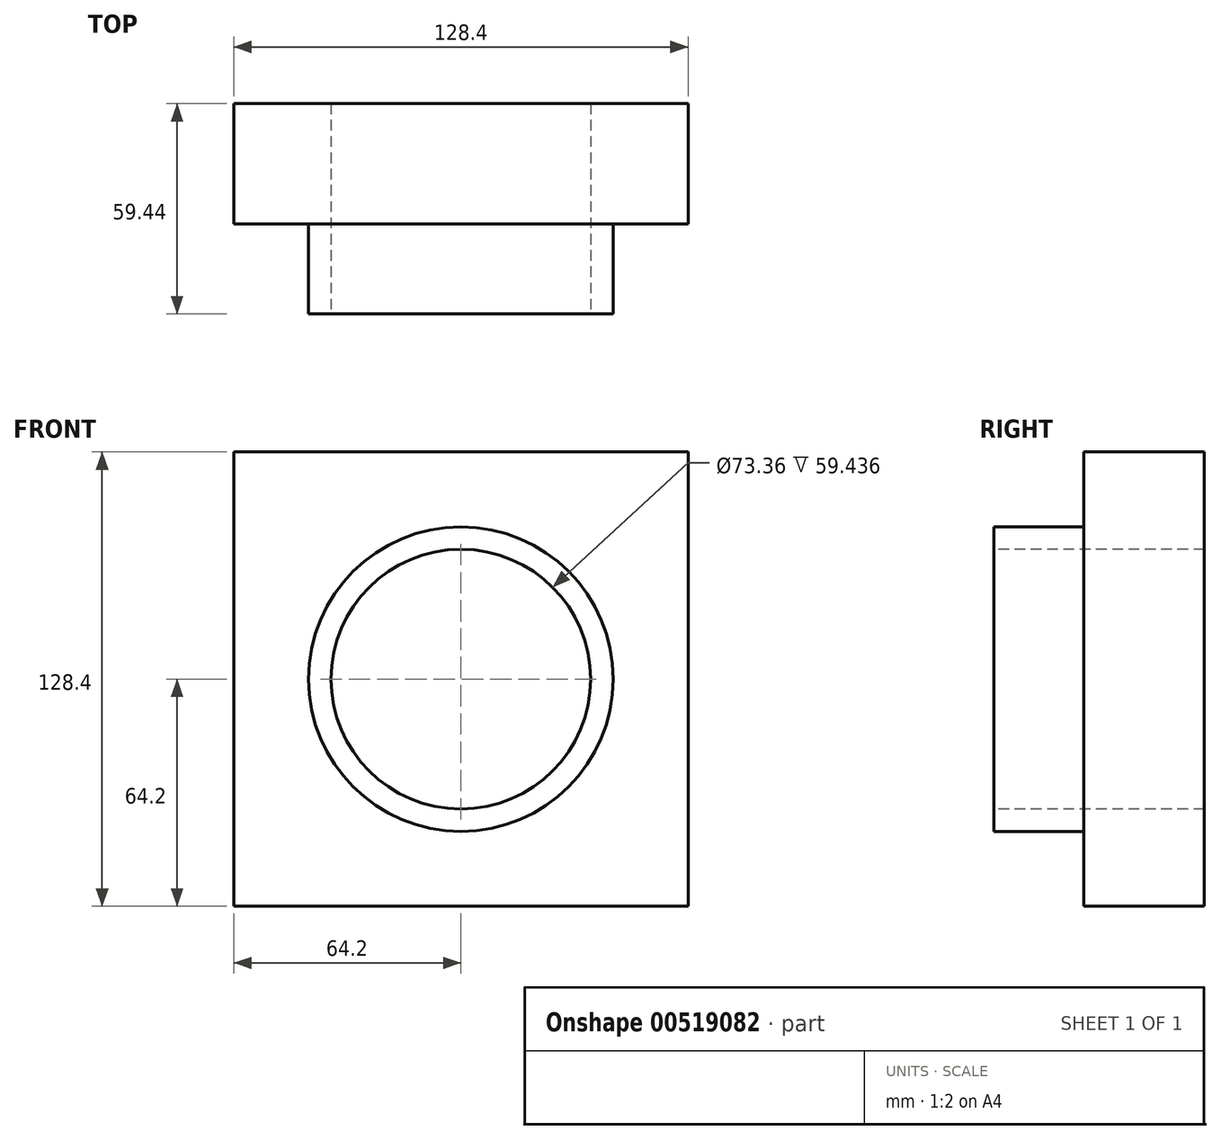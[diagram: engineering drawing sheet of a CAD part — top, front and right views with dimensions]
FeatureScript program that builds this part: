
annotation { "Feature Type Name" : "Feature", "Feature Type Description" : "" }
export const myFeature = defineFeature(function(context is Context, id is Id, definition is map)
    precondition{}
    {
        {
            var Q0;
            Q0=qCreatedBy(makeId("Front.planeOp"),FACE);
            var sketch = newSketch(context, id + "F0", { "sketchPlane" : qUnion([Q0])});
            skLineSegment(sketch, "E0.bottom", {"start": v(64.2, 64.2) * mm, "end": v(-64.2, 64.2) * mm});
            skLineSegment(sketch, "E0.top", {"start": v(64.2, -64.2) * mm, "end": v(-64.2, -64.2) * mm});
            skLineSegment(sketch, "E0.left", {"start": v(64.2, 64.2) * mm, "end": v(64.2, -64.2) * mm});
            skLineSegment(sketch, "E0.right", {"start": v(-64.2, 64.2) * mm, "end": v(-64.2, -64.2) * mm});
            skPoint(sketch, "E0.middle", {"position": v(0, 0) * mm});
            skSolve(sketch);
        }
        {
            var Q0;
            Q0=makeQuery(id+"F0.imprint","IMPRINT",FACE,{"disambiguationData":[TD([[makeQuery(id+"F0.imprint","IMPRINT",EDGE,{"derivedFrom":sQuery(id+"F0.wireOp",EDGE,"E0.bottom")}),1.0]])]});
            extrude(context, id + "F1", {"entities" : qUnion([Q0]), "depth" : 34.04 * mm, "offsetDistance" : 25.4 * mm});
        }
        {
            var Q0;
            Q0=makeQuery(id+"F1.opExtrude","CAP_FACE",FACE,{"disambiguationData":[OSD([sQuery(id+"F0.wireOp",EDGE,"E0.bottom"),sQuery(id+"F0.wireOp",EDGE,"E0.top"),sQuery(id+"F0.wireOp",EDGE,"E0.left"),sQuery(id+"F0.wireOp",EDGE,"E0.right")])],"isStart":false});
            var sketch = newSketch(context, id + "F2", { "sketchPlane" : qUnion([Q0])});
            skCircle(sketch, "E1", {"center": v(0, 0) * mm, "radius": 43.03 * mm});
            skSolve(sketch);
        }
        {
            var Q0;
            Q0=makeQuery(id+"F2.imprint","IMPRINT",FACE,{"disambiguationData":[TD([[makeQuery(id+"F2.imprint","IMPRINT",EDGE,{"derivedFrom":sQuery(id+"F2.wireOp",EDGE,"E1")}),1.0]])]});
            extrude(context, id + "F3", {"entities" : qUnion([Q0]), "operationType" : NewBodyOperationType.ADD, "depth" : 25.4 * mm, "offsetDistance" : 25.4 * mm});
        }
        {
            var Q0;
            Q0=makeQuery(id+"F3.opExtrude","CAP_FACE",FACE,{"disambiguationData":[OSD([sQuery(id+"F2.wireOp",EDGE,"E1")])],"isStart":false});
            var sketch = newSketch(context, id + "F4", { "sketchPlane" : qUnion([Q0])});
            skCircle(sketch, "E2.0", {"center": v(0, 0) * mm, "radius": 36.68 * mm});
            skSolve(sketch);
        }
        {
            var Q0;
            Q0=makeQuery(id+"F4.imprint","IMPRINT",FACE,{"disambiguationData":[TD([[makeQuery(id+"F4.imprint","IMPRINT",EDGE,{"derivedFrom":sQuery(id+"F4.wireOp",EDGE,"E2.0")}),1.0]])]});
            extrude(context, id + "F5", {"entities" : qUnion([Q0]), "operationType" : NewBodyOperationType.REMOVE, "oppositeDirection" : true, "depth" : 94.74 * mm, "offsetDistance" : 25.4 * mm});
        }
    });
